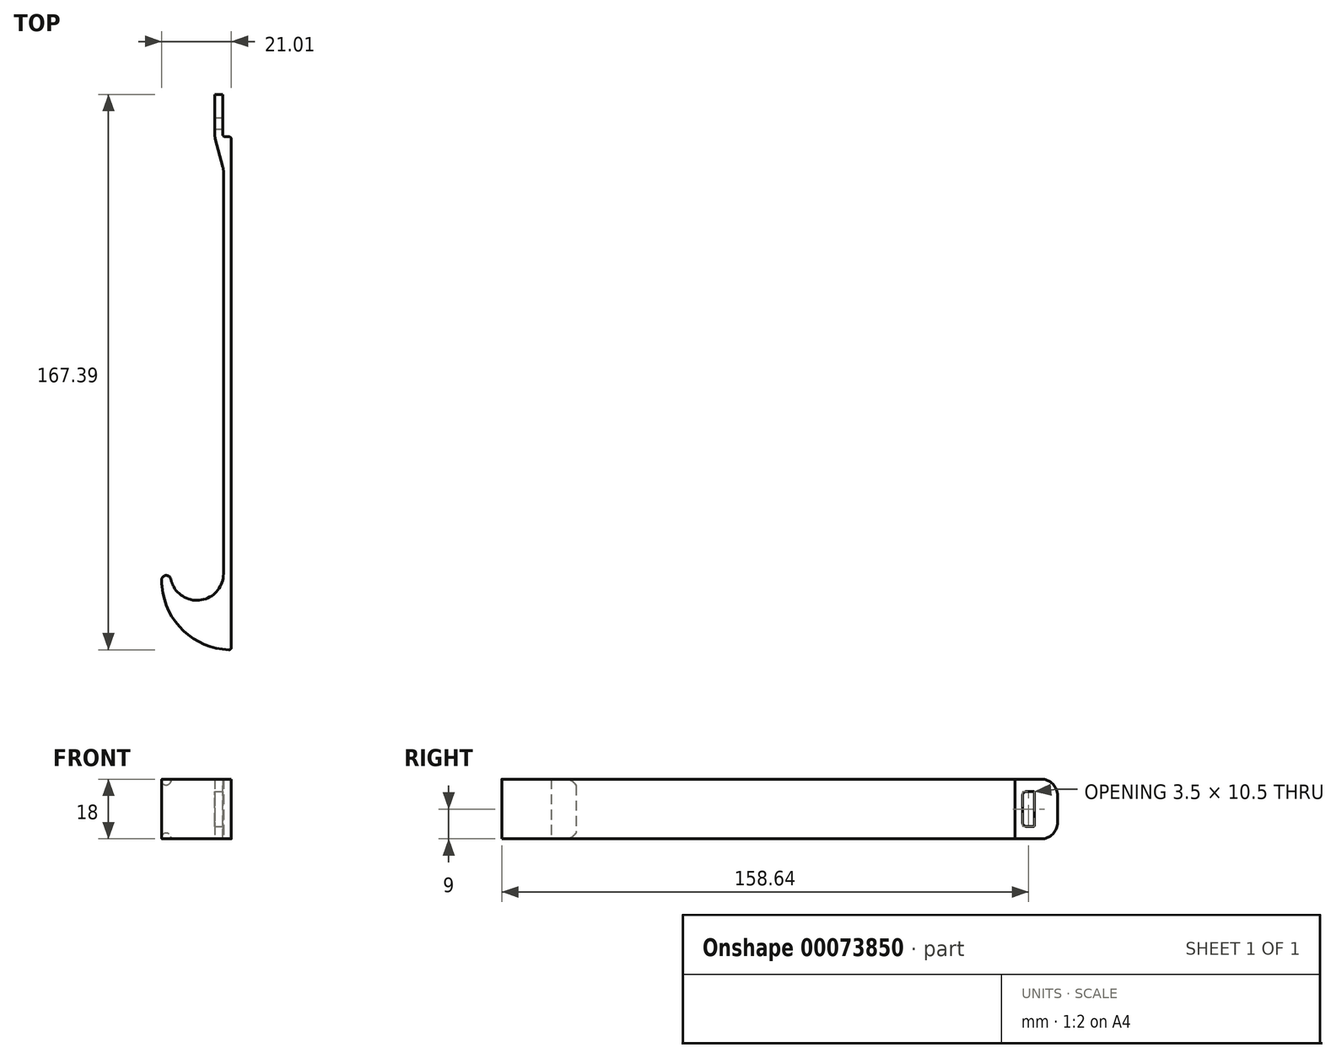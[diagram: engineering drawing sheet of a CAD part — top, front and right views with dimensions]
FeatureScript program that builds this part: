
annotation { "Feature Type Name" : "Feature", "Feature Type Description" : "" }
export const myFeature = defineFeature(function(context is Context, id is Id, definition is map)
    precondition{}
    {
        {
            var Q0;
            Q0=qCreatedBy(makeId("Top.planeOp"),FACE);
            var sketch = newSketch(context, id + "F0", { "sketchPlane" : qUnion([Q0])});
            skLineSegment(sketch, "E0", {"start": v(0, -7.5) * mm, "end": v(0, -129.5) * mm});
            skArc(sketch, "E1", {"start": v(-15.83, -131.12) * mm, "mid": v(-7.19, -137.46) * mm, "end": v(0, -129.5) * mm});
            skLineSegment(sketch, "E2", {"start": v(-15.83, -131.12) * mm, "end": v(-8, -129.5) * mm, "construction": true});
            skLineSegment(sketch, "E3", {"start": v(-8, -129.5) * mm, "end": v(0, -129.5) * mm, "construction": true});
            skArc(sketch, "E4", {"start": v(-15.83, -131.12) * mm, "mid": v(-17.35, -130) * mm, "end": v(-18.6, -131.4) * mm});
            skArc(sketch, "E5", {"start": v(-18.6, -131.4) * mm, "mid": v(-12.7, -146) * mm, "end": v(1.68, -152.4) * mm});
            skLineSegment(sketch, "E6", {"start": v(2.4, -151.7) * mm, "end": v(2.4, 1.5) * mm});
            skPoint(sketch, "E7.visualSharp", {"position": v(0, 0) * mm});
            skLineSegment(sketch, "E8", {"start": v(-18.6, -131.4) * mm, "end": v(-18.6, -129.5) * mm, "construction": true});
            skLineSegment(sketch, "E9", {"start": v(-18.6, -129.5) * mm, "end": v(-8, -129.5) * mm, "construction": true});
            skPoint(sketch, "E10.visualSharp", {"position": v(2.4, -152.4) * mm});
            skArc(sketch, "E10.filletArc", {"start": v(1.68, -152.4) * mm, "mid": v(2.19, -152.2) * mm, "end": v(2.4, -151.7) * mm});
            skLineSegment(sketch, "E11", {"start": v(-18.6, -130) * mm, "end": v(-15.83, -130) * mm, "construction": true});
            skLineSegment(sketch, "E12", {"start": v(-15.83, -130) * mm, "end": v(-15.83, -131.12) * mm, "construction": true});
            skLineSegment(sketch, "E13", {"start": v(-2.6, 2.2) * mm, "end": v(-2.6, 15) * mm});
            skLineSegment(sketch, "E14", {"start": v(-2.6, 15) * mm, "end": v(-0.2, 15) * mm});
            skLineSegment(sketch, "E15", {"start": v(-0.2, 15) * mm, "end": v(-0.2, 2.9) * mm});
            skLineSegment(sketch, "E16", {"start": v(0.5, 2.2) * mm, "end": v(1.7, 2.2) * mm});
            skLineSegment(sketch, "E17", {"start": v(1.68, -152.4) * mm, "end": v(2.4, -152.4) * mm, "construction": true});
            skLineSegment(sketch, "E18", {"start": v(2.4, -152.4) * mm, "end": v(2.4, -151.7) * mm, "construction": true});
            skPoint(sketch, "E19.visualSharp", {"position": v(2.4, 2.2) * mm});
            skArc(sketch, "E19.filletArc", {"start": v(2.4, 1.5) * mm, "mid": v(2.2, 2) * mm, "end": v(1.7, 2.2) * mm});
            skPoint(sketch, "E20.visualSharp", {"position": v(-0.2, 2.2) * mm});
            skArc(sketch, "E20.filletArc", {"start": v(-0.2, 2.9) * mm, "mid": v(0, 2.4) * mm, "end": v(0.5, 2.2) * mm});
            skLineSegment(sketch, "E21", {"start": v(-2.6, 2.2) * mm, "end": v(0, -7.5) * mm});
            skLineSegment(sketch, "E22", {"start": v(-2.6, 2.2) * mm, "end": v(0.5, 2.2) * mm, "construction": true});
            skSolve(sketch);
        }
        {
            var Q0;
            Q0 = qSketchRegion(id + "F0", true);
            extrude(context, id + "F1", {"entities" : qUnion([Q0]), "endBound" : BoundingType.SYMMETRIC, "depth" : 18 * mm});
        }
        {
            var Q0;
            Q0=makeQuery(id+"F1.opExtrude","SWEPT_EDGE",EDGE,{"disambiguationData":[OSD([sQuery(id+"F0.wireOp",EDGE,"E13"),sQuery(id+"F0.wireOp",EDGE,"E21")])]});
            var Q1;
            Q1=makeQuery(id+"F1.opExtrude","SWEPT_EDGE",EDGE,{"disambiguationData":[OSD([sQuery(id+"F0.wireOp",EDGE,"E0"),sQuery(id+"F0.wireOp",EDGE,"E21")])]});
            fillet(context, id + "F2", {"entities" : qUnion([Q0, Q1]), "radius" : 5 * mm, "tangentPropagation" : true, "allowEdgeOverflow" : false});
        }
        {
            var Q0;
            Q0=qCreatedBy(makeId("Right.planeOp"),FACE);
            var sketch = newSketch(context, id + "F3", { "sketchPlane" : qUnion([Q0])});
            skArc(sketch, "E23", {"start": v(-133.4, -9) * mm, "mid": v(-130.57, -7.83) * mm, "end": v(-129.4, -5) * mm});
            skLineSegment(sketch, "E24", {"start": v(-129.4, -5) * mm, "end": v(-129.4, 5) * mm});
            skArc(sketch, "E25", {"start": v(-129.4, 5) * mm, "mid": v(-130.57, 7.83) * mm, "end": v(-133.4, 9) * mm});
            skLineSegment(sketch, "E26", {"start": v(-133.4, -9) * mm, "end": v(-133.4, -10) * mm});
            skLineSegment(sketch, "E27", {"start": v(-133.4, -10) * mm, "end": v(-128.4, -10) * mm});
            skLineSegment(sketch, "E28", {"start": v(-128.4, -10) * mm, "end": v(-128.4, 10) * mm});
            skLineSegment(sketch, "E29", {"start": v(-128.4, 10) * mm, "end": v(-133.4, 10) * mm});
            skLineSegment(sketch, "E30", {"start": v(-133.4, 10) * mm, "end": v(-133.4, 9) * mm});
            skLineSegment(sketch, "E31", {"start": v(-133.4, -9) * mm, "end": v(-133.4, 9) * mm, "construction": true});
            skLineSegment(sketch, "E32", {"start": v(-128.4, 0) * mm, "end": v(-133.4, 0) * mm, "construction": true});
            skSolve(sketch);
        }
        {
            var Q0;
            Q0=qSketchRegion(id+"F3",true);
            extrude(context, id + "F4", {"entities" : qUnion([Q0]), "operationType" : NewBodyOperationType.REMOVE, "oppositeDirection" : true, "depth" : 30 * mm, "hasSecondDirection" : true, "secondDirectionOppositeDirection" : true, "secondDirectionDepth" : 10 * mm});
        }
        {
            var Q0;
            Q0=qCreatedBy(makeId("Right.planeOp"),FACE);
            var sketch = newSketch(context, id + "F5", { "sketchPlane" : qUnion([Q0])});
            skLineSegment(sketch, "E33", {"start": v(8, -4.95) * mm, "end": v(8, 4.95) * mm});
            skLineSegment(sketch, "E34", {"start": v(7.7, 5.25) * mm, "end": v(5.5, 5.25) * mm});
            skLineSegment(sketch, "E35", {"start": v(4.5, 4.25) * mm, "end": v(4.5, -4.25) * mm});
            skLineSegment(sketch, "E36", {"start": v(5.5, -5.25) * mm, "end": v(7.7, -5.25) * mm});
            skLineSegment(sketch, "E37", {"start": v(4.5, 0) * mm, "end": v(8, 0) * mm, "construction": true});
            skLineSegment(sketch, "E38", {"start": v(8, 5.25) * mm, "end": v(15, 5.25) * mm, "construction": true});
            skLineSegment(sketch, "E39", {"start": v(15, 5.25) * mm, "end": v(15, -5.25) * mm, "construction": true});
            skLineSegment(sketch, "E40", {"start": v(15, -5.25) * mm, "end": v(8, -5.25) * mm, "construction": true});
            skPoint(sketch, "E41.visualSharp", {"position": v(8, 5.25) * mm});
            skArc(sketch, "E41.filletArc", {"start": v(8, 4.95) * mm, "mid": v(7.91, 5.16) * mm, "end": v(7.7, 5.25) * mm});
            skPoint(sketch, "E42.visualSharp", {"position": v(8, -5.25) * mm});
            skArc(sketch, "E42.filletArc", {"start": v(7.7, -5.25) * mm, "mid": v(7.91, -5.16) * mm, "end": v(8, -4.95) * mm});
            skPoint(sketch, "E43.visualSharp", {"position": v(4.5, 5.25) * mm});
            skArc(sketch, "E43.filletArc", {"start": v(5.5, 5.25) * mm, "mid": v(4.8, 4.96) * mm, "end": v(4.5, 4.25) * mm});
            skPoint(sketch, "E44.visualSharp", {"position": v(4.5, -5.25) * mm});
            skArc(sketch, "E44.filletArc", {"start": v(4.5, -4.25) * mm, "mid": v(4.8, -4.96) * mm, "end": v(5.5, -5.25) * mm});
            skSolve(sketch);
        }
        {
            var Q0;
            Q0 = qSketchRegion(id + "F5", true);
            extrude(context, id + "F6", {"entities" : qUnion([Q0]), "operationType" : NewBodyOperationType.REMOVE, "oppositeDirection" : true, "depth" : 10 * mm});
        }
        {
            var Q0;
            Q0=makeQuery(id+"F1.opExtrude","CAP_EDGE",EDGE,{"disambiguationData":[OSD([sQuery(id+"F0.wireOp",EDGE,"E14")])],"isStart":true});
            var Q1;
            Q1=makeQuery(id+"F1.opExtrude","CAP_EDGE",EDGE,{"disambiguationData":[OSD([sQuery(id+"F0.wireOp",EDGE,"E14")])],"isStart":false});
            fillet(context, id + "F7", {"entities" : qUnion([Q0, Q1]), "radius" : 5 * mm, "tangentPropagation" : true, "allowEdgeOverflow" : false});
        }
    });
